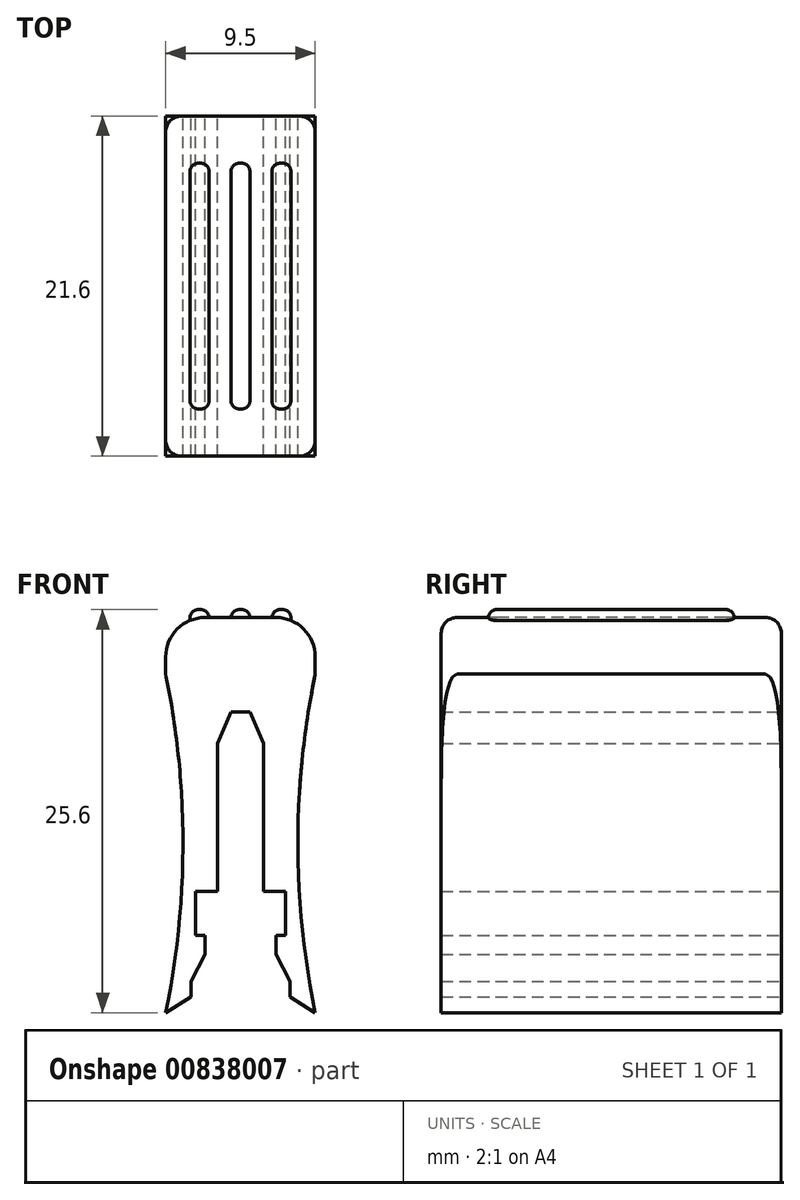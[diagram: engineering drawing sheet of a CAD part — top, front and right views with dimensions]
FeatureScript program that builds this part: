
annotation { "Feature Type Name" : "Feature", "Feature Type Description" : "" }
export const myFeature = defineFeature(function(context is Context, id is Id, definition is map)
    precondition{}
    {
        {
            var Q0;
            Q0=qCreatedBy(makeId("Front.planeOp"),FACE);
            var sketch = newSketch(context, id + "F0", { "sketchPlane" : qUnion([Q0])});
            skLineSegment(sketch, "E0.bottom", {"start": v(2.25, 12.55) * mm, "end": v(-4.75, 12.55) * mm});
            skLineSegment(sketch, "E0.top", {"start": v(4.75, -12.55) * mm, "end": v(-4.75, -12.55) * mm});
            skLineSegment(sketch, "E0.left", {"start": v(4.75, 10.05) * mm, "end": v(4.75, -12.55) * mm});
            skLineSegment(sketch, "E0.right", {"start": v(-4.75, 12.55) * mm, "end": v(-4.75, -12.55) * mm});
            skPoint(sketch, "E0.middle", {"position": v(0, 0) * mm});
            skLineSegment(sketch, "E1", {"start": v(0, 6.55) * mm, "end": v(-0.6, 6.55) * mm});
            skLineSegment(sketch, "E2", {"start": v(-0.6, 6.55) * mm, "end": v(-1.45, 4.55) * mm});
            skLineSegment(sketch, "E3", {"start": v(-1.45, 4.55) * mm, "end": v(-1.45, -4.85) * mm});
            skLineSegment(sketch, "E4", {"start": v(-1.45, -4.85) * mm, "end": v(-2.85, -4.85) * mm});
            skLineSegment(sketch, "E5", {"start": v(-2.85, -4.85) * mm, "end": v(-2.85, -7.65) * mm});
            skLineSegment(sketch, "E6", {"start": v(-2.85, -7.65) * mm, "end": v(-2.25, -7.65) * mm});
            skLineSegment(sketch, "E7", {"start": v(-2.25, -7.65) * mm, "end": v(-2.25, -8.85) * mm});
            skLineSegment(sketch, "E8", {"start": v(-2.25, -8.85) * mm, "end": v(-3.15, -10.55) * mm});
            skLineSegment(sketch, "E9", {"start": v(-3.15, -10.55) * mm, "end": v(-3.15, -11.55) * mm});
            skLineSegment(sketch, "E10", {"start": v(-3.15, -11.55) * mm, "end": v(-4.75, -12.55) * mm});
            skLineSegment(sketch, "E11.MirrorCS", {"start": v(0, 6.55) * mm, "end": v(0.6, 6.55) * mm});
            skLineSegment(sketch, "E12.MirrorCS", {"start": v(0.6, 6.55) * mm, "end": v(1.45, 4.55) * mm});
            skLineSegment(sketch, "E13.MirrorCS", {"start": v(1.45, 4.55) * mm, "end": v(1.45, -4.85) * mm});
            skLineSegment(sketch, "E14.MirrorCS", {"start": v(1.45, -4.85) * mm, "end": v(2.85, -4.85) * mm});
            skLineSegment(sketch, "E15.MirrorCS", {"start": v(2.85, -4.85) * mm, "end": v(2.85, -7.65) * mm});
            skLineSegment(sketch, "E16.MirrorCS", {"start": v(2.85, -7.65) * mm, "end": v(2.25, -7.65) * mm});
            skLineSegment(sketch, "E17.MirrorCS", {"start": v(2.25, -7.65) * mm, "end": v(2.25, -8.85) * mm});
            skLineSegment(sketch, "E18.MirrorCS", {"start": v(2.25, -8.85) * mm, "end": v(3.15, -10.55) * mm});
            skLineSegment(sketch, "E19.MirrorCS", {"start": v(3.15, -10.55) * mm, "end": v(3.15, -11.55) * mm});
            skLineSegment(sketch, "E20.MirrorCS", {"start": v(3.15, -11.55) * mm, "end": v(4.75, -12.55) * mm});
            skCircle(sketch, "E21", {"center": v(56.73, -1.8) * mm, "radius": 53.08 * mm});
            skPoint(sketch, "E22", {"position": v(4.75, -12.55) * mm});
            skCircle(sketch, "E23.MirrorC", {"center": v(-56.73, -1.8) * mm, "radius": 53.08 * mm});
            skPoint(sketch, "E24", {"position": v(4.75, 8.95) * mm});
            skPoint(sketch, "E25.visualSharp", {"position": v(4.75, 12.55) * mm});
            skArc(sketch, "E25.filletArc", {"start": v(4.75, 10.05) * mm, "mid": v(4.02, 11.82) * mm, "end": v(2.25, 12.55) * mm});
            skArc(sketch, "E26.MirrorCS", {"start": v(-4.75, 10.05) * mm, "mid": v(-4.02, 11.82) * mm, "end": v(-2.25, 12.55) * mm});
            skSolve(sketch);
        }
        {
            var Q0;
            Q0=makeQuery(id+"F0.imprint","IMPRINT",FACE,{"disambiguationData":[TD([[makeQuery(id+"F0.imprint","IMPRINT",EDGE,{"derivedFrom":sQuery(id+"F0.wireOp",EDGE,"E1")}),-1.0]])]});
            extrude(context, id + "F1", {"entities" : qUnion([Q0]), "depth" : 21.6 * mm, "offsetDistance" : 25 * mm});
        }
        {
            var Q0;
            Q0=makeQuery(id+"F1.opExtrude","CAP_EDGE",EDGE,{"disambiguationData":[OSD([sQuery(id+"F0.wireOp",EDGE,"E0.bottom")])],"isStart":true});
            var Q1;
            Q1=makeQuery(id+"F1.opExtrude","CAP_EDGE",EDGE,{"disambiguationData":[OSD([sQuery(id+"F0.wireOp",EDGE,"E0.bottom")])],"isStart":false});
            fillet(context, id + "F2", {"entities" : qUnion([Q0, Q1]), "radius" : 1 * mm, "tangentPropagation" : true, "allowEdgeOverflow" : false});
        }
        {
            var Q0;
            Q0=makeQuery(id+"F1.opExtrude","SWEPT_FACE",FACE,{"disambiguationData":[OSD([sQuery(id+"F0.wireOp",EDGE,"E0.bottom")])]});
            var sketch = newSketch(context, id + "F3", { "sketchPlane" : qUnion([Q0])});
            skLineSegment(sketch, "E27.bottom", {"start": v(-0.1, -3) * mm, "end": v(0.1, -3) * mm});
            skLineSegment(sketch, "E27.top", {"start": v(-0.1, -18.6) * mm, "end": v(0.1, -18.6) * mm});
            skLineSegment(sketch, "E27.left", {"start": v(-0.6, -3.5) * mm, "end": v(-0.6, -18.1) * mm});
            skLineSegment(sketch, "E27.right", {"start": v(0.6, -3.5) * mm, "end": v(0.6, -18.1) * mm});
            skPoint(sketch, "E27.middle", {"position": v(0, -10.8) * mm});
            skLineSegment(sketch, "E28", {"start": v(-1.3, -18.57) * mm, "end": v(-1.3, -2.75) * mm, "construction": true});
            skLineSegment(sketch, "E29.MirrorCS", {"start": v(-2, -3.5) * mm, "end": v(-2, -18.1) * mm});
            skLineSegment(sketch, "E30.MirrorCS", {"start": v(-2.5, -3) * mm, "end": v(-2.7, -3) * mm});
            skLineSegment(sketch, "E31.MirrorCS", {"start": v(-3.2, -3.5) * mm, "end": v(-3.2, -18.1) * mm});
            skLineSegment(sketch, "E32.MirrorCS", {"start": v(-2.5, -18.6) * mm, "end": v(-2.7, -18.6) * mm});
            skLineSegment(sketch, "E33.MirrorCS", {"start": v(2, -3.5) * mm, "end": v(2, -18.1) * mm});
            skLineSegment(sketch, "E34.MirrorCS", {"start": v(2.5, -3) * mm, "end": v(2.7, -3) * mm});
            skLineSegment(sketch, "E35.MirrorCS", {"start": v(2.5, -18.6) * mm, "end": v(2.7, -18.6) * mm});
            skLineSegment(sketch, "E36.MirrorCS", {"start": v(3.2, -3.5) * mm, "end": v(3.2, -18.1) * mm});
            skPoint(sketch, "E37.visualSharp", {"position": v(-3.2, -18.6) * mm});
            skArc(sketch, "E37.filletArc", {"start": v(-3.2, -18.1) * mm, "mid": v(-3.05, -18.45) * mm, "end": v(-2.7, -18.6) * mm});
            skPoint(sketch, "E38.visualSharp", {"position": v(-2, -18.6) * mm});
            skArc(sketch, "E38.filletArc", {"start": v(-2.5, -18.6) * mm, "mid": v(-2.15, -18.45) * mm, "end": v(-2, -18.1) * mm});
            skPoint(sketch, "E39.visualSharp", {"position": v(-2, -3) * mm});
            skArc(sketch, "E39.filletArc", {"start": v(-2, -3.5) * mm, "mid": v(-2.15, -3.15) * mm, "end": v(-2.5, -3) * mm});
            skPoint(sketch, "E40.visualSharp", {"position": v(-3.2, -3) * mm});
            skArc(sketch, "E40.filletArc", {"start": v(-2.7, -3) * mm, "mid": v(-3.05, -3.15) * mm, "end": v(-3.2, -3.5) * mm});
            skPoint(sketch, "E41.visualSharp", {"position": v(-0.6, -3) * mm});
            skArc(sketch, "E41.filletArc", {"start": v(-0.1, -3) * mm, "mid": v(-0.45, -3.15) * mm, "end": v(-0.6, -3.5) * mm});
            skPoint(sketch, "E42.visualSharp", {"position": v(0.6, -3) * mm});
            skArc(sketch, "E42.filletArc", {"start": v(0.6, -3.5) * mm, "mid": v(0.45, -3.15) * mm, "end": v(0.1, -3) * mm});
            skPoint(sketch, "E43.visualSharp", {"position": v(3.2, -18.6) * mm});
            skArc(sketch, "E43.filletArc", {"start": v(2.7, -18.6) * mm, "mid": v(3.05, -18.45) * mm, "end": v(3.2, -18.1) * mm});
            skPoint(sketch, "E44.visualSharp", {"position": v(2, -18.6) * mm});
            skArc(sketch, "E44.filletArc", {"start": v(2, -18.1) * mm, "mid": v(2.15, -18.45) * mm, "end": v(2.5, -18.6) * mm});
            skPoint(sketch, "E45.visualSharp", {"position": v(0.6, -18.6) * mm});
            skArc(sketch, "E45.filletArc", {"start": v(0.1, -18.6) * mm, "mid": v(0.45, -18.45) * mm, "end": v(0.6, -18.1) * mm});
            skPoint(sketch, "E46.visualSharp", {"position": v(-0.6, -18.6) * mm});
            skArc(sketch, "E46.filletArc", {"start": v(-0.6, -18.1) * mm, "mid": v(-0.45, -18.45) * mm, "end": v(-0.1, -18.6) * mm});
            skPoint(sketch, "E47.visualSharp", {"position": v(2, -3) * mm});
            skArc(sketch, "E47.filletArc", {"start": v(2.5, -3) * mm, "mid": v(2.15, -3.15) * mm, "end": v(2, -3.5) * mm});
            skPoint(sketch, "E48.visualSharp", {"position": v(3.2, -3) * mm});
            skArc(sketch, "E48.filletArc", {"start": v(3.2, -3.5) * mm, "mid": v(3.05, -3.15) * mm, "end": v(2.7, -3) * mm});
            skSolve(sketch);
        }
        {
            var Q0;
            {var subQ4=sQuery(id+"F3.wireOp",EDGE,"E34.MirrorCS");Q0=makeQuery(id+"F3.imprint","IMPRINT",FACE,{"disambiguationData":[TD([[makeQuery(id+"F3.imprint","IMPRINT",EDGE,{"derivedFrom":subQ4}),-1.0]])]});}
            var Q1;
            {var subQ0=sQuery(id+"F3.wireOp",EDGE,"E33.MirrorCS");Q1=makeQuery(id+"F3.imprint","IMPRINT",FACE,{"disambiguationData":[TD([[makeQuery(id+"F3.imprint","IMPRINT",EDGE,{"derivedFrom":subQ0}),1.0]])]});}
            var Q2;
            Q2=makeQuery(id+"F3.imprint","IMPRINT",FACE,{"disambiguationData":[TD([[makeQuery(id+"F3.imprint","IMPRINT",EDGE,{"derivedFrom":sQuery(id+"F3.wireOp",EDGE,"E27.bottom")}),-1.0]])]});
            var Q3;
            {var subQ0=sQuery(id+"F3.wireOp",EDGE,"E29.MirrorCS");Q3=makeQuery(id+"F3.imprint","IMPRINT",FACE,{"disambiguationData":[TD([[makeQuery(id+"F3.imprint","IMPRINT",EDGE,{"derivedFrom":subQ0}),-1.0]])]});}
            var Q4;
            {var subQ1=sQuery(id+"F3.wireOp",EDGE,"E30.MirrorCS");Q4=makeQuery(id+"F3.imprint","IMPRINT",FACE,{"disambiguationData":[TD([[makeQuery(id+"F3.imprint","IMPRINT",EDGE,{"derivedFrom":subQ1}),1.0]])]});}
            extrude(context, id + "F4", {"entities" : qUnion([Q0, Q1, Q2, Q3, Q4]), "operationType" : NewBodyOperationType.ADD, "endBound" : BoundingType.SYMMETRIC, "depth" : 1 * mm, "offsetDistance" : 25 * mm});
        }
        {
            var Q0;
            Q0=makeQuery(id+"F4.opExtrude","CAP_FACE",FACE,{"disambiguationData":[OSD([sQuery(id+"F3.wireOp",EDGE,"E29.MirrorCS"),sQuery(id+"F3.wireOp",EDGE,"E30.MirrorCS"),sQuery(id+"F3.wireOp",EDGE,"E31.MirrorCS"),sQuery(id+"F3.wireOp",EDGE,"E32.MirrorCS"),sQuery(id+"F3.wireOp",EDGE,"E37.filletArc"),sQuery(id+"F3.wireOp",EDGE,"E38.filletArc"),sQuery(id+"F3.wireOp",EDGE,"E39.filletArc"),sQuery(id+"F3.wireOp",EDGE,"E40.filletArc")])],"isStart":false});
            var Q1;
            Q1=makeQuery(id+"F4.opExtrude","CAP_FACE",FACE,{"disambiguationData":[OSD([sQuery(id+"F3.wireOp",EDGE,"E27.bottom"),sQuery(id+"F3.wireOp",EDGE,"E27.top"),sQuery(id+"F3.wireOp",EDGE,"E27.left"),sQuery(id+"F3.wireOp",EDGE,"E27.right"),sQuery(id+"F3.wireOp",EDGE,"E41.filletArc"),sQuery(id+"F3.wireOp",EDGE,"E42.filletArc"),sQuery(id+"F3.wireOp",EDGE,"E45.filletArc"),sQuery(id+"F3.wireOp",EDGE,"E46.filletArc")])],"isStart":false});
            var Q2;
            Q2=makeQuery(id+"F4.opExtrude","CAP_FACE",FACE,{"disambiguationData":[OSD([sQuery(id+"F3.wireOp",EDGE,"E33.MirrorCS"),sQuery(id+"F3.wireOp",EDGE,"E34.MirrorCS"),sQuery(id+"F3.wireOp",EDGE,"E35.MirrorCS"),sQuery(id+"F3.wireOp",EDGE,"E36.MirrorCS"),sQuery(id+"F3.wireOp",EDGE,"E43.filletArc"),sQuery(id+"F3.wireOp",EDGE,"E44.filletArc"),sQuery(id+"F3.wireOp",EDGE,"E47.filletArc"),sQuery(id+"F3.wireOp",EDGE,"E48.filletArc")])],"isStart":false});
            fillet(context, id + "F5", {"entities" : qUnion([Q0, Q1, Q2]), "radius" : 0.5 * mm, "tangentPropagation" : true, "allowEdgeOverflow" : false});
        }
    });
